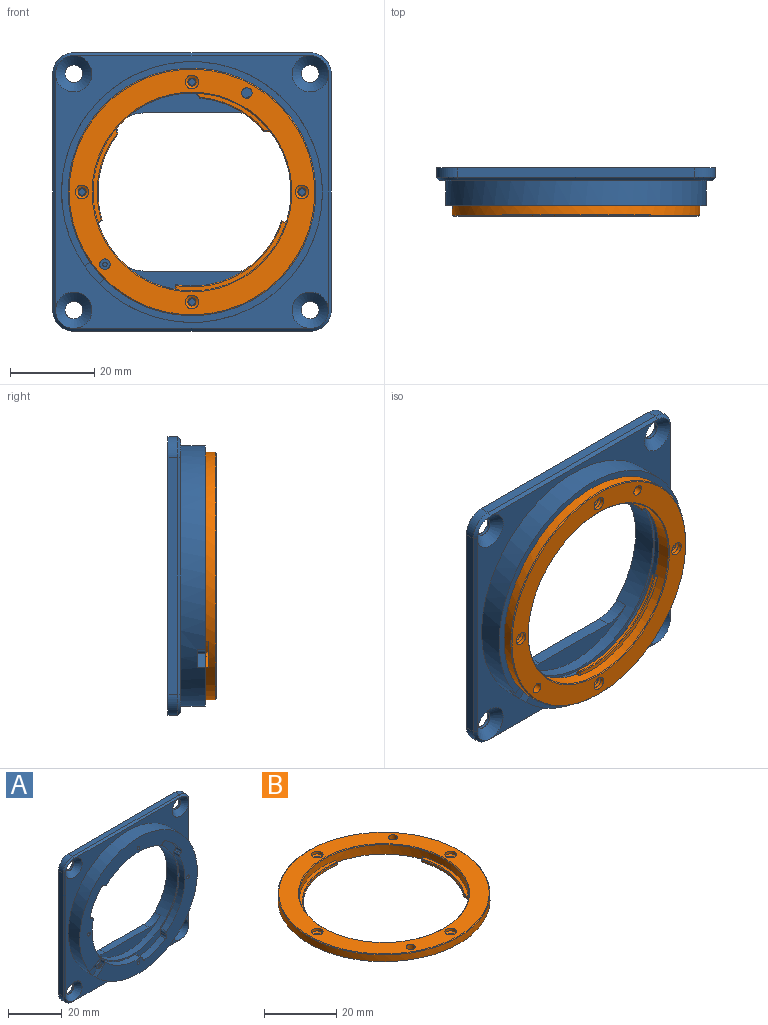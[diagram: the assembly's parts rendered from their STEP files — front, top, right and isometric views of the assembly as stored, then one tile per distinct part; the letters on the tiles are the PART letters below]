
ASSEMBLY  parts=2 mates=1
PART A: 79 faces, bbox 66x8.9x66 mm
  f0: plane 61.8x61.8mm, normal (0,-1,0), area 1014.8mm2, adj f1,f2,f18,f39,f41,f43,f45,f47
  f1: cylinder r=24.33mm len=27.83mm, axis (0,-1,0), area 89.8mm2, adj f0,f40,f74,f76
  f2: cylinder r=24.33mm len=30.68mm, axis (0,-1,0), area 102.5mm2, adj f0,f40,f70,f71
  f3: cylinder r=23.73mm len=47.45mm, axis (0,1,0), area 641.9mm2, adj f17,f32,f34,f35,f36,f37,f38,f40
  f4: plane 56x2.3mm, normal (0,0,-1), area 128.8mm2, adj f5,f11,f17,f28
  f5: cylinder r=5mm len=5mm, axis (0,1,0), area 18.1mm2, adj f4,f6,f17,f30
  f6: plane 56x2.3mm, normal (1,0,0), area 128.8mm2, adj f5,f7,f17,f29
  f7: cylinder r=5mm len=5mm, axis (0,1,0), area 18.1mm2, adj f6,f8,f17,f27
  f8: plane 56x2.3mm, normal (0,0,1), area 128.8mm2, adj f7,f9,f17,f25
  f9: cylinder r=5mm len=5mm, axis (0,1,0), area 18.1mm2, adj f8,f10,f17,f23
  f10: plane 56x2.3mm, normal (-1,0,0), area 128.8mm2, adj f9,f11,f17,f24
  f11: cylinder r=5mm len=5mm, axis (0,1,0), area 18.1mm2, adj f4,f10,f17,f26
  f12: cylinder r=2.1mm len=4.2mm, axis (0,1,0), area 10.6mm2, adj f17,f21
  f13: cylinder r=2.1mm len=4.2mm, axis (0,1,0), area 10.6mm2, adj f17,f22
  f14: cylinder r=2.1mm len=4.2mm, axis (0,1,0), area 10.6mm2, adj f17,f19
  f15: cylinder r=2.1mm len=4.2mm, axis (0,1,0), area 10.6mm2, adj f17,f20
  f16: plane 64.6x64.6mm, normal (0,-1,0), area 925.3mm2, adj f18,f19,f20,f21,f22,f24,f25,f28
  f17: plane 66x66mm, normal (0,1,0), area 2714.2mm2, adj f3,f4,f5,f6,f7,f8,f9,f10
  f18: cylinder r=30.9mm len=61.8mm, axis (0,1,0), area 1129mm2, adj f0,f16,f49,f52,f54
  f19: cone r=2.1mm half-angle=45deg, axis (0,-1,0), area 62.6mm2, adj f14,f16,f30
  f20: cone r=4.3mm half-angle=45deg, axis (0,-1,0), area 62.6mm2, adj f15,f16,f26
  f21: cone r=2.1mm half-angle=45deg, axis (0,-1,0), area 62.6mm2, adj f12,f16,f23
  f22: cone r=4.3mm half-angle=45deg, axis (0,-1,0), area 62.6mm2, adj f13,f16,f27
  f23: cone r=4.3mm half-angle=45deg, axis (0,1,0), area 7.2mm2, adj f9,f21,f24,f25
  f24: plane 56x0.7mm, normal (-0.71,-0.71,0), area 55.4mm2, adj f10,f16,f23,f26
  f25: plane 56x0.7mm, normal (0,-0.71,0.71), area 55.4mm2, adj f8,f16,f23,f27
  f26: cone r=4.3mm half-angle=45deg, axis (0,1,0), area 7.2mm2, adj f11,f20,f24,f28
  f27: cone r=4.3mm half-angle=45deg, axis (0,1,0), area 7.2mm2, adj f7,f22,f25,f29
  f28: plane 56x0.7mm, normal (0,-0.71,-0.71), area 55.4mm2, adj f4,f16,f26,f30
  f29: plane 56x0.7mm, normal (0.71,-0.71,0), area 55.4mm2, adj f6,f16,f27,f30
  f30: cone r=4.3mm half-angle=45deg, axis (0,1,0), area 7.2mm2, adj f5,f19,f28,f29
  f31: plane 23x3mm, normal (0,0,1), area 69mm2, adj f17,f32,f35,f36
  f32: plane 34.7x7.54mm, normal (0,-1,0), area 101.9mm2, adj f3,f31,f35,f36
  f33: plane 23x3mm, normal (0,0,-1), area 69mm2, adj f17,f34,f37,f38
  f34: plane 34.7x7.54mm, normal (0,-1,0), area 101.9mm2, adj f3,f33,f37,f38
  f35: cylinder r=8mm len=5.85mm, axis (0,1,0), area 19.7mm2, adj f3,f17,f31,f32
  f36: cylinder r=8mm len=5.85mm, axis (0,1,0), area 19.7mm2, adj f3,f17,f31,f32
  f37: cylinder r=8mm len=5.85mm, axis (0,1,0), area 19.7mm2, adj f3,f17,f33,f34
  f38: cylinder r=8mm len=5.85mm, axis (0,1,0), area 19.7mm2, adj f3,f17,f33,f34
  f39: cylinder r=24.33mm len=29.69mm, axis (0,-1,0), area 128.4mm2, adj f0,f40,f50,f51,f54,f69,f77
  f40: plane 50.62x49.68mm, normal (0,-1,0), area 177.2mm2, adj f1,f2,f3,f39,f58,f59,f60,f61
  f41: cylinder r=0.75mm len=5mm, axis (0,-1,0), area 23.6mm2, adj f0,f42
  f42: plane 1.5x1.5mm, normal (0,-1,0), area 1.8mm2, adj f41
  f43: cylinder r=0.75mm len=5mm, axis (0,-1,0), area 23.6mm2, adj f0,f44
  f44: plane 1.5x1.5mm, normal (0,-1,0), area 1.8mm2, adj f43
  f45: cylinder r=0.75mm len=5mm, axis (0,-1,0), area 23.6mm2, adj f0,f46
  f46: plane 1.5x1.5mm, normal (0,-1,0), area 1.8mm2, adj f45
  f47: cylinder r=0.75mm len=5mm, axis (0,-1,0), area 23.6mm2, adj f0,f48
  f48: plane 1.5x1.5mm, normal (0,-1,0), area 1.8mm2, adj f47
  f49: plane 3.6x3.58mm, normal (-0.7,0,0.71), area 10.2mm2, adj f0,f18,f50,f54
  f50: cylinder r=2mm len=2mm, axis (0,-1,0), area 3.4mm2, adj f0,f39,f49,f54
  f51: cylinder r=2mm len=2mm, axis (0,-1,0), area 3.4mm2, adj f0,f39,f52,f54
  f52: plane 4.18x2.88mm, normal (0.57,0,-0.82), area 10.2mm2, adj f0,f18,f51,f54
  f53: cylinder r=1.25mm len=2.5mm, axis (0,-1,0), area 15.7mm2, adj f54,f55
  f54: plane 7.73x7.49mm, normal (0,-1,0), area 27mm2, adj f18,f39,f49,f50,f51,f52,f53
  f55: plane 2.5x2.5mm, normal (0,-1,0), area 4mm2, adj f53,f56
  f56: cylinder r=0.53mm len=2mm, axis (0,-1,0), area 6.6mm2, adj f55,f57
  f57: plane 1.05x1.05mm, normal (0,-1,0), area 0.9mm2, adj f56
  f58: plane 3x0.14mm, normal (-0.82,0,-0.57), area 0.5mm2, adj f0,f40,f67,f70
  f59: plane 3x0.17mm, normal (1,0,0.09), area 0.5mm2, adj f0,f40,f68,f69
  f60: cylinder r=26.5mm len=10.99mm, axis (0,-1,0), area 35.4mm2, adj f0,f40,f67,f68
  f61: plane 3x0.15mm, normal (-0.5,0,0.87), area 0.5mm2, adj f0,f40,f71,f72
  f62: cylinder r=26.5mm len=8.27mm, axis (0,-1,0), area 35.4mm2, adj f0,f40,f72,f73
  f63: plane 3x0.15mm, normal (0.87,0,-0.5), area 0.5mm2, adj f0,f40,f73,f74
  f64: cylinder r=26.5mm len=10.13mm, axis (0,-1,0), area 35.4mm2, adj f0,f40,f75,f78
  f65: plane 3x0.17mm, normal (0.26,0,0.97), area 0.5mm2, adj f0,f40,f77,f78
  f66: plane 3x0.12mm, normal (-0.71,0,-0.71), area 0.5mm2, adj f0,f40,f75,f76
  f67: cylinder r=1mm len=3mm, axis (0,-1,0), area 4.8mm2, adj f0,f40,f58,f60
  f68: cylinder r=1mm len=3mm, axis (0,-1,0), area 4.8mm2, adj f0,f40,f59,f60
  f69: cylinder r=1mm len=3mm, axis (0,-1,0), area 4.6mm2, adj f0,f39,f40,f59
  f70: cylinder r=1mm len=3mm, axis (0,-1,0), area 4.6mm2, adj f0,f2,f40,f58
  f71: cylinder r=1mm len=3mm, axis (0,-1,0), area 4.6mm2, adj f0,f2,f40,f61
  f72: cylinder r=1mm len=3mm, axis (0,-1,0), area 4.8mm2, adj f0,f40,f61,f62
  f73: cylinder r=1mm len=3mm, axis (0,-1,0), area 4.8mm2, adj f0,f40,f62,f63
  f74: cylinder r=1mm len=3mm, axis (0,-1,0), area 4.6mm2, adj f0,f1,f40,f63
  f75: cylinder r=1mm len=3mm, axis (0,-1,0), area 4.8mm2, adj f0,f40,f64,f66
  f76: cylinder r=1mm len=3mm, axis (0,-1,0), area 4.6mm2, adj f0,f1,f40,f66
  f77: cylinder r=1mm len=3mm, axis (0,-1,0), area 4.6mm2, adj f0,f39,f40,f65
  f78: cylinder r=1mm len=3mm, axis (0,-1,0), area 4.8mm2, adj f0,f40,f64,f65
PART B: 48 faces, bbox 58.6x58.6x3.4 mm
  f0: cylinder r=1.25mm len=2.5mm, axis (0,0,-1), area 14.1mm2, adj f9,f47
  f1: plane 58.6x58.6mm, normal (0,0,-1), area 762.9mm2, adj f2,f3,f4,f5,f7,f8,f22,f43
  f2: cylinder r=1mm len=2mm, axis (0,0,-1), area 7.8mm2, adj f1,f39
  f3: cylinder r=1mm len=2mm, axis (0,0,-1), area 7.8mm2, adj f1,f41
  f4: cylinder r=1mm len=2mm, axis (0,0,-1), area 7.8mm2, adj f1,f35
  f5: cylinder r=1mm len=2mm, axis (0,0,-1), area 7.8mm2, adj f1,f37
  f6: cylinder r=23.45mm len=46.9mm, axis (0,0,-1), area 401.1mm2, adj f10,f11,f12,f14,f15,f17,f18,f20
  f7: cylinder r=1.25mm len=2.5mm, axis (0,0,-1), area 19.6mm2, adj f1,f9
  f8: cylinder r=29.3mm len=58.6mm, axis (0,0,-1), area 417.8mm2, adj f1,f33,f44,f45,f47
  f9: plane 58.2x58.2mm, normal (0,0,1), area 861.2mm2, adj f0,f7,f33,f34,f36,f38,f40,f42
  f10: plane 26.11x16.37mm, normal (0,0,1), area 30.9mm2, adj f6,f27,f28,f29
  f11: plane 17.33x8.96mm, normal (0,0,1), area 17.9mm2, adj f6,f30,f31,f32
  f12: plane 22.16x5.63mm, normal (0,0,1), area 21.4mm2, adj f6,f24,f25,f26
  f13: cylinder r=22.3mm len=15.16mm, axis (0,0,1), area 12.3mm2, adj f14,f21,f23,f31
  f14: plane 1.21x1.02mm, normal (0.76,0.65,0), area 1.1mm2, adj f6,f13,f23,f30
  f15: plane 1.58x0.7mm, normal (-0.99,-0.12,0), area 1.1mm2, adj f6,f16,f23,f25
  f16: cylinder r=22.3mm len=20.35mm, axis (0,0,1), area 15mm2, adj f15,f17,f23,f26
  f17: plane 1x0.7mm, normal (-0.54,0.84,0), area 0.8mm2, adj f6,f16,f23,f24
  f18: plane 1.13x0.7mm, normal (0.99,-0.17,0), area 0.8mm2, adj f6,f19,f23,f28
  f19: cylinder r=22.3mm len=25.08mm, axis (0,0,1), area 22.4mm2, adj f18,f20,f23,f29
  f20: plane 1.09x0.7mm, normal (-0.31,-0.95,0), area 0.8mm2, adj f6,f19,f23,f27
  f21: plane 1.58x0.7mm, normal (0.08,1,0), area 1.1mm2, adj f6,f13,f23,f32
  f22: cylinder r=24.45mm len=48.9mm, axis (0,0,1), area 143.1mm2, adj f1,f23,f43,f46,f47
  f23: plane 48.9x48.9mm, normal (0,0,-1), area 236.3mm2, adj f6,f13,f14,f15,f16,f17,f18,f19
  f24: cylinder r=0.2mm len=1.11mm, axis (0.84,0.54,0), area 0.4mm2, adj f6,f12,f17,f26
  f25: cylinder r=0.2mm len=1.6mm, axis (-0.12,0.99,0), area 0.5mm2, adj f6,f12,f15,f26
  f26: torus R=22.5mm, axis (0,0,-1), area 6.7mm2, adj f12,f16,f24,f25
  f27: cylinder r=0.2mm len=1.16mm, axis (-0.95,0.31,0), area 0.3mm2, adj f6,f10,f20,f29
  f28: cylinder r=0.2mm len=1.17mm, axis (-0.17,-0.99,0), area 0.3mm2, adj f6,f10,f18,f29
  f29: torus R=22.5mm, axis (0,0,-1), area 10mm2, adj f10,f19,f27,f28
  f30: cylinder r=0.2mm len=1.34mm, axis (0.65,-0.76,0), area 0.5mm2, adj f6,f11,f14,f31
  f31: torus R=22.5mm, axis (0,0,-1), area 5.5mm2, adj f11,f13,f30,f32
  f32: cylinder r=0.2mm len=1.6mm, axis (1,-0.08,0), area 0.5mm2, adj f6,f11,f21,f31
  f33: cone r=29.1mm half-angle=45deg, axis (0,0,-1), area 51.9mm2, adj f8,f9
  f34: cone r=23.45mm half-angle=45deg, axis (0,0,1), area 41.9mm2, adj f6,f9
  f35: cone r=0mm half-angle=59deg, axis (0,0,1), area 5.7mm2, adj f4,f36
  f36: cylinder r=1.6mm len=3.2mm, axis (0,0,1), area 9mm2, adj f9,f35
  f37: cone r=0mm half-angle=59deg, axis (0,0,1), area 5.7mm2, adj f5,f38
  f38: cylinder r=1.6mm len=3.2mm, axis (0,0,1), area 9mm2, adj f9,f37
  f39: cone r=0mm half-angle=59deg, axis (0,0,1), area 5.7mm2, adj f2,f40
  f40: cylinder r=1.6mm len=3.2mm, axis (0,0,1), area 9mm2, adj f9,f39
  f41: cone r=0mm half-angle=59deg, axis (0,0,1), area 5.7mm2, adj f3,f42
  f42: cylinder r=1.6mm len=3.2mm, axis (0,0,1), area 9mm2, adj f9,f41
  f43: cylinder r=1mm len=1.03mm, axis (0,0,-1), area 0.8mm2, adj f1,f22,f44,f47
  f44: plane 3.01x2.49mm, normal (0.64,-0.77,0), area 2.7mm2, adj f1,f8,f43,f47
  f45: plane 3.01x2.49mm, normal (-0.64,0.77,0), area 2.7mm2, adj f1,f8,f46,f47
  f46: cylinder r=1mm len=1.07mm, axis (0,0,-1), area 0.8mm2, adj f1,f22,f45,f47
  f47: plane 8.88x8.47mm, normal (0,0,-1), area 33.7mm2, adj f0,f8,f22,f43,f44,f45,f46
PLACE A t=(3.93,6.06,-0.97)mm fixed
PLACE B rot(axis=(0,-0.71,0.71),180deg) t=(3.93,-2.82,-0.97)mm
MATE fastened A.f1 <-> B.f6  axis (0,-1,0) through (3.93,-2.82,-0.97)mm
